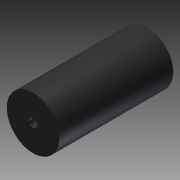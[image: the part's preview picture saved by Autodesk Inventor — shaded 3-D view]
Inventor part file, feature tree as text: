
AUTODESK INVENTOR PART (.ipt)
format: ipt  version: 2012 (Build 160160000, 160)  size: 74,240 bytes
history: native  units: in
note: dims shown in document units (in); Inventor stores cm internally (conversion verified against a paired STEP export)
features: extrude x1, sketch x1
ambient origin geometry x8: Origin, YZ Plane, XZ Plane, XY Plane, X Axis, Y Axis, Z Axis, Center Point
bodies: Solid1 (feature_tree)
feature tree (2):
  extrude  "Extrusion1"  Depth=0.5in
  sketch  "Sketch1"  dims[d0=3.0in d1=0.5in d2=6.5in d3=0.0in]
